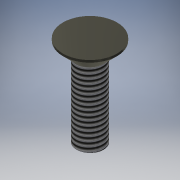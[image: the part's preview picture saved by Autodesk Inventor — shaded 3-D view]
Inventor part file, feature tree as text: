
AUTODESK INVENTOR PART (.ipt)
format: ipt  version: 2020.2 (Build 242310000, 310)  size: 130,048 bytes
history: native  units: mm
features: extrude x4, sketch x4, other x1, thread x1, chamfer x1
ambient origin geometry x1: Origin
bodies: Body1 (feature_tree)
feature tree (11):
  other  "ソリッド1"
  extrude  "押し出し1"  Depth=3.0mm
  extrude  "押し出し2"  Depth=6.0mm TaperAngle=0.0deg
  thread  "ねじ1"
  chamfer  "面取り1"  Distance=6.0mm
  extrude  "押し出し4"  Depth=1.75mm TaperAngle=0.0deg
  extrude  "押し出し5"  Depth=10.0mm TaperAngle=0.0deg
  sketch  "スケッチ1"
  sketch  "スケッチ2"
  sketch  "スケッチ4"
  sketch  "スケッチ5"
